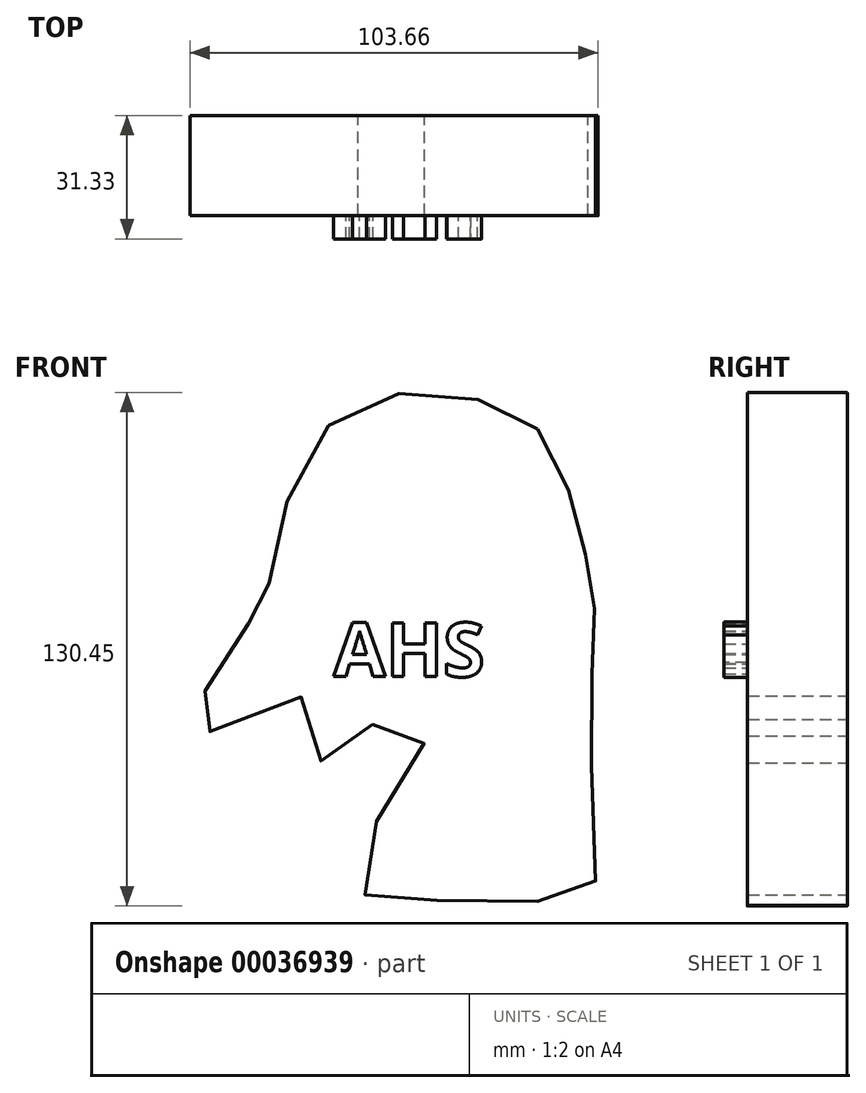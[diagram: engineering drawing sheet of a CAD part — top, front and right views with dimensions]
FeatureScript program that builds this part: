
annotation { "Feature Type Name" : "Feature", "Feature Type Description" : "" }
export const myFeature = defineFeature(function(context is Context, id is Id, definition is map)
    precondition{}
    {
        {
            var Q0;
            Q0=qCreatedBy(makeId("Front.planeOp"),FACE);
            var sketch = newSketch(context, id + "F0", { "sketchPlane" : qUnion([Q0])});
            skFitSpline(sketch, "E0", {"points": [v(-64.29, 37.2) * mm, v(-57.63, 64.42) * mm, v(-40.7, 83.17) * mm, v(-17.12, 84.98) * mm, v(1.03, 78.94) * mm, v(10.1, 65.63) * mm, v(15.54, 46.88) * mm, v(17.36, 37.81) * mm, v(18.57, 21.48) * mm, v(16.75, 0.92) * mm, v(16.75, -42.62) * mm, v(-7.44, -42.02) * mm, v(-37.68, -43.83) * mm, v(-40.1, -28.71) * mm, v(-24.98, -2.1) * mm, v(-37.68, 1.53) * mm, v(-50.98, -8.15) * mm, v(-55.82, 8.18) * mm, v(-83.64, -1.5) * mm, v(-73.96, 20.88) * mm, v(-67.92, 29.35) * mm, v(-64.29, 37.2) * mm]});
            skSolve(sketch);
        }
        {
            var Q0;
            Q0=makeQuery(id+"F0.imprint","IMPRINT",FACE,{"disambiguationData":[TD([[makeQuery(id+"F0.imprint","IMPRINT",EDGE,{"derivedFrom":sQuery(id+"F0.wireOp",EDGE,"E0")}),-1.0]])]});
            extrude(context, id + "F1", {"entities" : qUnion([Q0]), "depth" : 25.4 * mm});
        }
        {
            var Q0;
            Q0=qCreatedBy(makeId("Front.planeOp"),FACE);
            var sketch = newSketch(context, id + "F2", { "sketchPlane" : qUnion([Q0])});
            skText(sketch, "E1", { "text": "AHS", "fontName": "OpenSans-Bold.ttf"});
            const initialGuessF2  = {"E1": [-0.04795, 0.0135, 1, 0, 0.01377]};
            skSetInitialGuess(sketch, initialGuessF2);
            skSolve(sketch);
        }
        {
            var Q0;
            Q0 = qSketchRegion(id + "F2", true);
            extrude(context, id + "F3", {"entities" : qUnion([Q0]), "operationType" : NewBodyOperationType.ADD, "depth" : 31.33 * mm});
        }
    });
